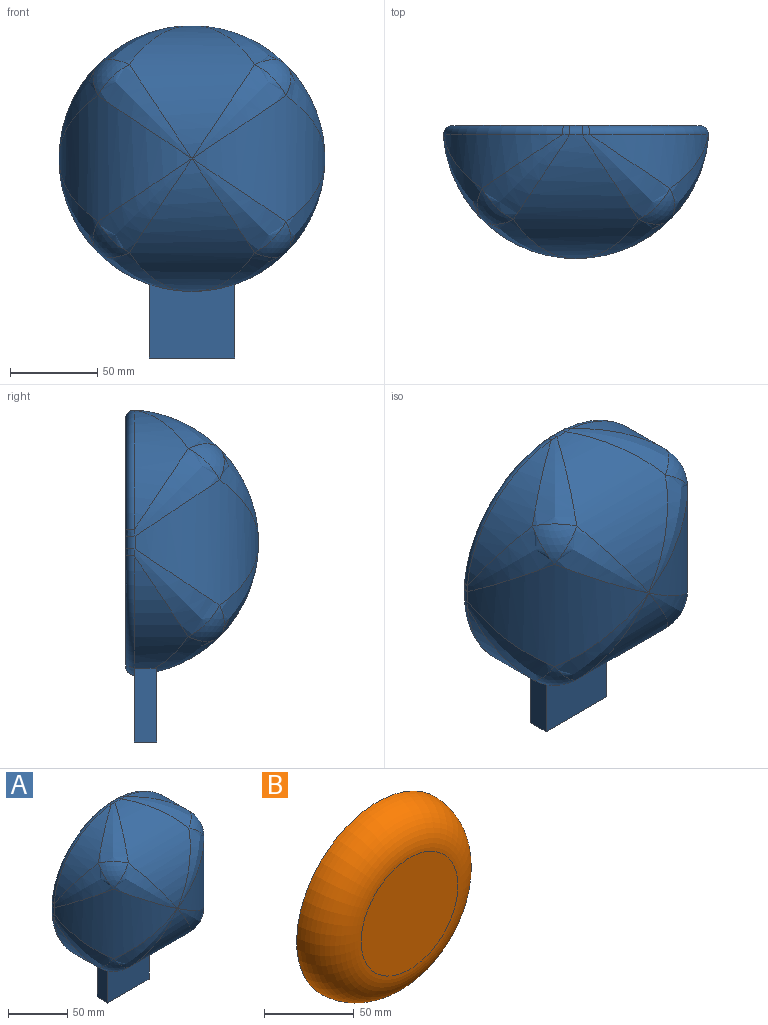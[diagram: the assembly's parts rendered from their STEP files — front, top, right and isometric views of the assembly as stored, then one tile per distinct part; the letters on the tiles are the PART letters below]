
ASSEMBLY  parts=2 mates=1
PART A: 51 faces, bbox 164.1x76.2x196.4 mm
  f0: cylinder r=76.2mm len=64.5mm, axis (0,1,0), area 1538.6mm2, adj f1,f48,f49,f50
  f1: torus R=71.12mm, axis (0,-1,0), area 813.1mm2, adj f0,f2,f42,f43,f47
  f2: plane 49.22x42.18mm, normal (0,1,0), area 1941.5mm2, adj f1,f3,f5,f40,f41,f50
  f3: plane 49.22x12.7mm, normal (0,0,-1), area 625.1mm2, adj f2,f4,f5,f50
  f4: plane 49.22x42.18mm, normal (0,-1,0), area 1941.5mm2, adj f3,f5,f41,f50
  f5: plane 42.18x12.7mm, normal (1,0,0), area 535.7mm2, adj f2,f3,f4,f6,f41
  f6: cylinder r=76.2mm len=64.5mm, axis (0,1,0), area 1538.6mm2, adj f5,f7,f39,f40
  f7: bspline ~55.65x55.65mm, area 927.2mm2, adj f6,f8,f37,f38
  f8: sphere r=25.4mm, area 338.7mm2, adj f7,f9,f39
  f9: bspline ~55.65x55.65mm, area 621mm2, adj f8,f10,f37
  f10: cylinder r=76.2mm len=76.01mm, axis (1,0,0), area 4301.3mm2, adj f9,f11,f35,f39,f49
  f11: bspline ~55.65x55.65mm, area 621mm2, adj f10,f12,f13
  f12: sphere r=25.4mm, area 338.7mm2, adj f11,f48,f49
  f13: cylinder r=76.2mm len=76.01mm, axis (0,0,1), area 4301.3mm2, adj f11,f14,f33,f34,f48
  f14: bspline ~55.65x55.65mm, area 659.8mm2, adj f13,f15,f31
  f15: sphere r=25.4mm, area 338.7mm2, adj f14,f16,f34
  f16: bspline ~50.25x50.25mm, area 927.3mm2, adj f15,f17,f20,f31
  f17: cylinder r=76.2mm len=68.2mm, axis (0,1,0), area 1610.4mm2, adj f16,f18,f34
  f18: torus R=71.12mm, axis (0,-1,0), area 813.1mm2, adj f17,f19,f20,f43
  f19: bspline ~10.55x6.31mm, area 31.1mm2, adj f18,f33,f34,f43
  f20: bspline ~12.47x6.41mm, area 31.2mm2, adj f16,f18,f21,f43
  f21: cylinder r=5.08mm len=7.26mm, axis (1,0,0), area 60.5mm2, adj f20,f22,f31,f43
  f22: bspline ~10.55x6.31mm, area 31.1mm2, adj f21,f23,f30,f43
  f23: torus R=71.12mm, axis (0,-1,0), area 813.1mm2, adj f22,f24,f28,f43
  f24: cylinder r=76.2mm len=68.2mm, axis (0,1,0), area 1610.4mm2, adj f23,f25,f30
  f25: bspline ~50.25x50.25mm, area 927.2mm2, adj f24,f26,f28,f37
  f26: sphere r=25.4mm, area 416.2mm2, adj f25,f27,f30
  f27: bspline ~47.36x47.36mm, area 495.2mm2, adj f26,f31,f37
  f28: bspline ~12.47x6.41mm, area 31.2mm2, adj f23,f25,f29,f43
  f29: cylinder r=5.08mm len=7.26mm, axis (0,0,1), area 60.5mm2, adj f28,f37,f38,f43
  f30: bspline ~55.65x55.65mm, area 927.3mm2, adj f22,f24,f26,f31
  f31: cylinder r=76.2mm len=76.01mm, axis (1,0,0), area 4301.3mm2, adj f14,f16,f21,f27,f30,f32
  f32: bspline ~24.51x24.51mm, area 13.7mm2, adj f31,f37
  f33: cylinder r=5.08mm len=7.26mm, axis (0,0,1), area 60.5mm2, adj f13,f19,f43,f47
  f34: bspline ~55.65x55.65mm, area 927.3mm2, adj f13,f15,f17,f19
  f35: cylinder r=5.08mm len=7.26mm, axis (1,0,0), area 60.5mm2, adj f10,f36,f42,f43
  f36: bspline ~12.47x6.41mm, area 31.2mm2, adj f35,f39,f40,f43
  f37: cylinder r=76.2mm len=76.01mm, axis (0,0,1), area 4301.3mm2, adj f7,f9,f25,f27,f29,f32
  f38: bspline ~10.55x6.31mm, area 31.1mm2, adj f7,f29,f40,f43
  f39: bspline ~55.65x55.65mm, area 927.2mm2, adj f6,f8,f10,f36,f41
  f40: torus R=71.12mm, axis (0,-1,0), area 813.1mm2, adj f2,f6,f36,f38,f43
  f41: cylinder r=76.2mm len=49.22mm, axis (0,1,0), area 439.1mm2, adj f2,f4,f5,f39,f49,f50
  f42: bspline ~10.55x6.31mm, area 31.1mm2, adj f1,f35,f43,f49
  f43: plane 141.89x141.89mm, normal (0,1,0), area 1109.6mm2, adj f1,f18,f19,f20,f21,f22,f23,f28
  f44: torus R=68.58mm, axis (0,-1,0), area 3276.3mm2, adj f43,f45
  f45: cylinder r=63.5mm len=127mm, axis (0,1,0), area 8107.3mm2, adj f44,f46
  f46: plane 127x127mm, normal (0,1,0), area 12667.7mm2, adj f45
  f47: bspline ~12.47x6.41mm, area 31.2mm2, adj f1,f33,f43,f48
  f48: bspline ~50.25x50.25mm, area 927.3mm2, adj f0,f12,f13,f47
  f49: bspline ~55.65x55.65mm, area 927.2mm2, adj f0,f10,f12,f41,f42
  f50: plane 42.18x12.7mm, normal (-1,0,0), area 535.7mm2, adj f0,f2,f3,f4,f41
PART B: 3 faces, bbox 137.5x25.4x137.5 mm
  f0: plane 76.2x76.2mm, normal (0,-1,0), area 4560.4mm2, adj f2
  f1: plane 127x127mm, normal (0,1,0), area 12667.7mm2, adj f2
  f2: torus R=38.1mm, axis (0,-1,0), area 13604.9mm2, adj f0,f1
PLACE A at identity
PLACE B rot(axis=(0,0,1),180deg) t=(0,-25.4,0)mm
MATE fastened B.f2 <-> A.f0  axis (0,-1,0) through (0,-25.4,0)mm
